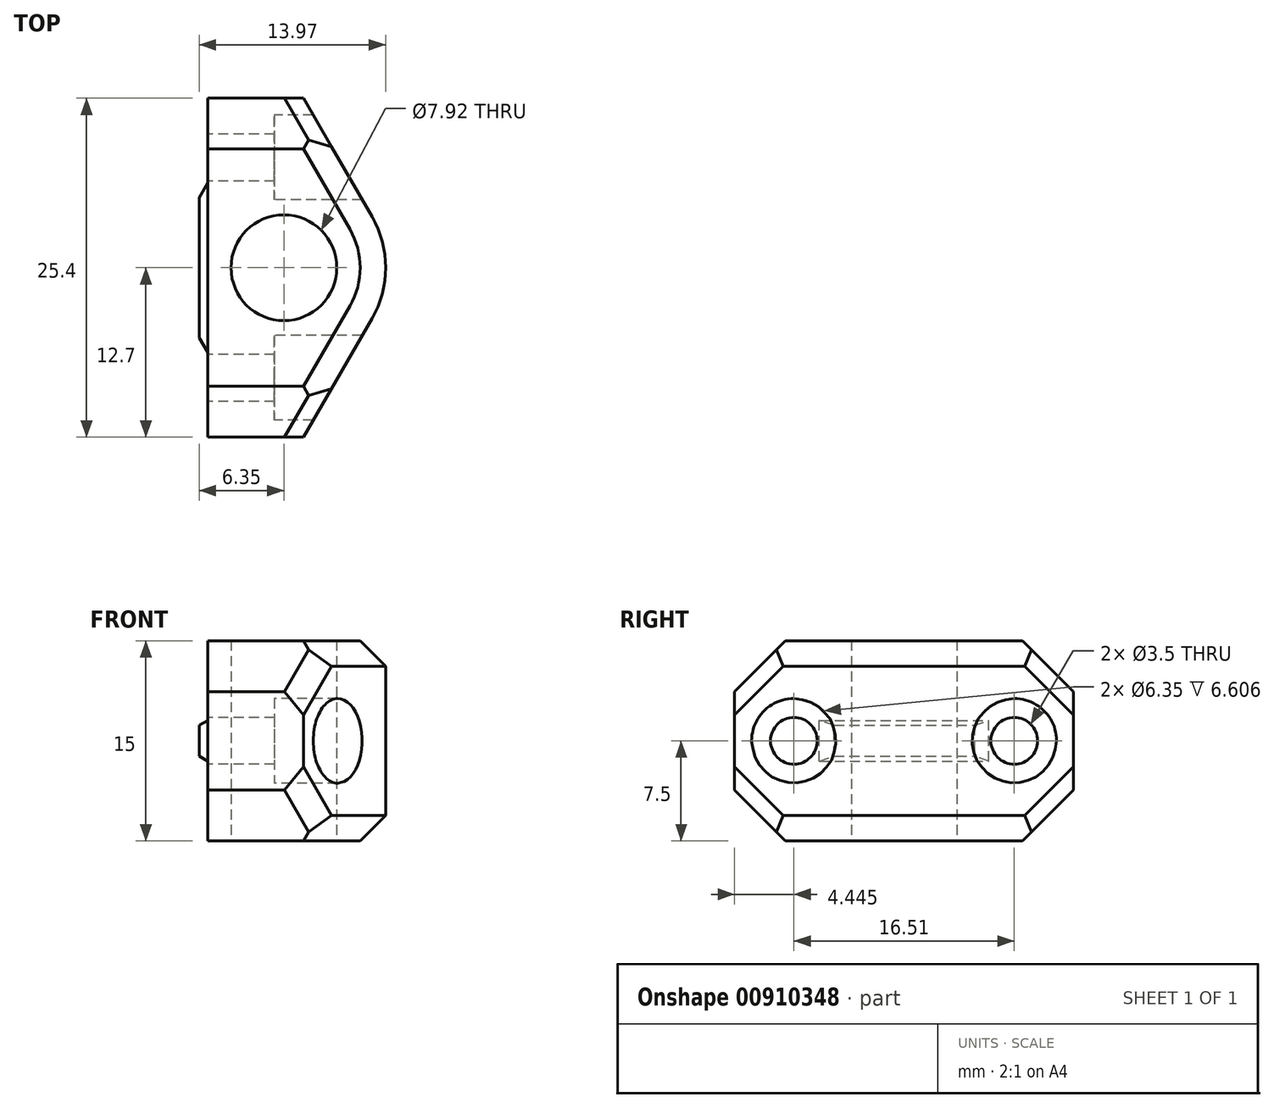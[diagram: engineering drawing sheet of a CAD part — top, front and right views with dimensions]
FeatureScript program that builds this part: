
annotation { "Feature Type Name" : "Feature", "Feature Type Description" : "" }
export const myFeature = defineFeature(function(context is Context, id is Id, definition is map)
    precondition{}
    {
        {
            var Q0;
            Q0=qCreatedBy(makeId("Top.planeOp"),FACE);
            var sketch = newSketch(context, id + "F0", { "sketchPlane" : qUnion([Q0])});
            skCircle(sketch, "E0", {"center": v(0, 0) * mm, "radius": 3.96 * mm});
            skLineSegment(sketch, "E1", {"start": v(-5.72, 12.7) * mm, "end": v(-5.72, -12.7) * mm});
            skLineSegment(sketch, "E2", {"start": v(-5.72, -12.7) * mm, "end": v(1.47, -12.7) * mm});
            skLineSegment(sketch, "E3", {"start": v(1.47, -12.7) * mm, "end": v(6.6, -3.81) * mm});
            skLineSegment(sketch, "E4", {"start": v(6.6, 3.8) * mm, "end": v(1.47, 12.7) * mm});
            skLineSegment(sketch, "E5", {"start": v(1.47, 12.7) * mm, "end": v(-5.72, 12.7) * mm});
            skArc(sketch, "E6", {"start": v(6.6, -3.81) * mm, "mid": v(7.62, 0) * mm, "end": v(6.6, 3.8) * mm});
            skLineSegment(sketch, "E7", {"start": v(-5.72, 6.6) * mm, "end": v(-0.72, 6.6) * mm, "construction": true});
            skLineSegment(sketch, "E8", {"start": v(-0.72, 6.6) * mm, "end": v(-0.72, 5.08) * mm, "construction": true});
            skLineSegment(sketch, "E9", {"start": v(-0.72, 5.08) * mm, "end": v(5.87, 5.08) * mm, "construction": true});
            skLineSegment(sketch, "E10", {"start": v(-5.72, 9.9) * mm, "end": v(-0.72, 9.9) * mm, "construction": true});
            skLineSegment(sketch, "E11", {"start": v(-0.72, 9.9) * mm, "end": v(-0.72, 11.43) * mm, "construction": true});
            skLineSegment(sketch, "E12", {"start": v(-0.72, 11.43) * mm, "end": v(2.2, 11.43) * mm, "construction": true});
            skLineSegment(sketch, "E13", {"start": v(-0.72, 9.9) * mm, "end": v(-0.72, 6.6) * mm, "construction": true});
            skLineSegment(sketch, "E14", {"start": v(-0.72, 8.26) * mm, "end": v(-5.72, 8.26) * mm, "construction": true});
            skSolve(sketch);
        }
        {
            var Q0;
            Q0 = qSketchRegion(id + "F0", true);
            extrude(context, id + "F1", {"entities" : qUnion([Q0]), "depth" : 15 * mm, "offsetDistance" : 25.4 * mm, "symmetric" : true});
        }
        {
            var Q0;
            Q0=makeQuery(id+"F1.opExtrude","SWEPT_FACE",FACE,{"disambiguationData":[OSD([sQuery(id+"F0.wireOp",EDGE,"E1")])]});
            var sketch = newSketch(context, id + "F2", { "sketchPlane" : qUnion([Q0])});
            skPoint(sketch, "E15", {"position": v(-8.26, 0) * mm});
            skPoint(sketch, "E16", {"position": v(8.26, 0) * mm});
            skLineSegment(sketch, "E17", {"start": v(-8.26, 0) * mm, "end": v(8.26, 0) * mm, "construction": true});
            skCircle(sketch, "E18", {"center": v(8.26, 0) * mm, "radius": 1.75 * mm});
            skCircle(sketch, "E19", {"center": v(-8.26, 0) * mm, "radius": 1.75 * mm});
            skSolve(sketch);
        }
        {
            var Q0;
            Q0 = qSketchRegion(id + "F2", true);
            extrude(context, id + "F3", {"entities" : qUnion([Q0]), "operationType" : NewBodyOperationType.REMOVE, "oppositeDirection" : true, "depth" : 5 * mm, "offsetDistance" : 25.4 * mm});
        }
        {
            var Q0;
            Q0=makeQuery(id+"F3.boolean.opBoolean","COPY",FACE,{"derivedFrom":makeQuery(id+"F3.opExtrude","CAP_FACE",FACE,{"disambiguationData":[OSD([sQuery(id+"F2.wireOp",EDGE,"E18")])],"isStart":false})});
            var sketch = newSketch(context, id + "F4", { "sketchPlane" : qUnion([Q0])});
            skCircle(sketch, "E20", {"center": v(8.26, 0) * mm, "radius": 3.18 * mm});
            skCircle(sketch, "E21", {"center": v(-8.26, 0) * mm, "radius": 3.18 * mm});
            skSolve(sketch);
        }
        {
            var Q0;
            Q0 = qSketchRegion(id + "F4", true);
            extrude(context, id + "F5", {"entities" : qUnion([Q0]), "operationType" : NewBodyOperationType.REMOVE, "endBound" : BoundingType.THROUGH_ALL, "oppositeDirection" : true, "depth" : 25.4 * mm, "offsetDistance" : 25.4 * mm});
        }
        {
            var Q0;
            Q0=makeQuery(id+"F1.opExtrude","CAP_EDGE",EDGE,{"disambiguationData":[OSD([sQuery(id+"F0.wireOp",EDGE,"E5")])],"isStart":true});
            var Q1;
            Q1=makeQuery(id+"F1.opExtrude","CAP_EDGE",EDGE,{"disambiguationData":[OSD([sQuery(id+"F0.wireOp",EDGE,"E5")])],"isStart":false});
            var Q2;
            Q2=makeQuery(id+"F1.opExtrude","CAP_EDGE",EDGE,{"disambiguationData":[OSD([sQuery(id+"F0.wireOp",EDGE,"E2")])],"isStart":false});
            var Q3;
            Q3=makeQuery(id+"F1.opExtrude","CAP_EDGE",EDGE,{"disambiguationData":[OSD([sQuery(id+"F0.wireOp",EDGE,"E2")])],"isStart":true});
            chamfer(context, id + "F6", {"entities" : qUnion([Q0, Q1, Q2, Q3]), "width" : 3.8 * mm, "tangentPropagation" : true});
        }
        {
            var Q0;
            Q0=makeQuery(id+"F1.opExtrude","CAP_EDGE",EDGE,{"disambiguationData":[OSD([sQuery(id+"F0.wireOp",EDGE,"E3")])],"isStart":true});
            var Q1;
            Q1=makeQuery(id+"F1.opExtrude","CAP_EDGE",EDGE,{"disambiguationData":[OSD([sQuery(id+"F0.wireOp",EDGE,"E3")])],"isStart":false});
            var Q2;
            Q2=makeQuery(id+"F6.opChamfer","BLEND_EDGE",EDGE,{"blendedFrom":[makeQuery(id+"F1.opExtrude","CAP_EDGE",EDGE,{"disambiguationData":[OSD([sQuery(id+"F0.wireOp",EDGE,"E2")])],"isStart":false}),makeQuery(id+"F1.opExtrude","SWEPT_FACE",FACE,{"disambiguationData":[OSD([sQuery(id+"F0.wireOp",EDGE,"E3")])]})],"blendedInto":[makeQuery(id+"F1.opExtrude","SWEPT_FACE",FACE,{"disambiguationData":[OSD([sQuery(id+"F0.wireOp",EDGE,"E3")])]})]});
            var Q3;
            Q3=makeQuery(id+"F6.opChamfer","BLEND_EDGE",EDGE,{"blendedFrom":[makeQuery(id+"F1.opExtrude","CAP_EDGE",EDGE,{"disambiguationData":[OSD([sQuery(id+"F0.wireOp",EDGE,"E2")])],"isStart":true}),makeQuery(id+"F1.opExtrude","SWEPT_FACE",FACE,{"disambiguationData":[OSD([sQuery(id+"F0.wireOp",EDGE,"E3")])]})],"blendedInto":[makeQuery(id+"F1.opExtrude","SWEPT_FACE",FACE,{"disambiguationData":[OSD([sQuery(id+"F0.wireOp",EDGE,"E3")])]})]});
            var Q4;
            Q4=makeQuery(id+"F6.opChamfer","BLEND_EDGE",EDGE,{"blendedFrom":[makeQuery(id+"F1.opExtrude","CAP_EDGE",EDGE,{"disambiguationData":[OSD([sQuery(id+"F0.wireOp",EDGE,"E5")])],"isStart":true}),makeQuery(id+"F1.opExtrude","SWEPT_FACE",FACE,{"disambiguationData":[OSD([sQuery(id+"F0.wireOp",EDGE,"E4")])]})],"blendedInto":[makeQuery(id+"F1.opExtrude","SWEPT_FACE",FACE,{"disambiguationData":[OSD([sQuery(id+"F0.wireOp",EDGE,"E4")])]})]});
            var Q5;
            Q5=makeQuery(id+"F6.opChamfer","BLEND_EDGE",EDGE,{"blendedFrom":[makeQuery(id+"F1.opExtrude","CAP_EDGE",EDGE,{"disambiguationData":[OSD([sQuery(id+"F0.wireOp",EDGE,"E5")])],"isStart":false}),makeQuery(id+"F1.opExtrude","SWEPT_FACE",FACE,{"disambiguationData":[OSD([sQuery(id+"F0.wireOp",EDGE,"E4")])]})],"blendedInto":[makeQuery(id+"F1.opExtrude","SWEPT_FACE",FACE,{"disambiguationData":[OSD([sQuery(id+"F0.wireOp",EDGE,"E4")])]})]});
            chamfer(context, id + "F7", {"entities" : qUnion([Q0, Q1, Q2, Q3, Q4, Q5]), "width" : 1.9 * mm, "tangentPropagation" : true});
        }
        {
            var Q0;
            Q0=qCreatedBy(makeId("Front.planeOp"),FACE);
            var sketch = newSketch(context, id + "F8", { "sketchPlane" : qUnion([Q0])});
            skLineSegment(sketch, "E22", {"start": v(-5.72, 1.52) * mm, "end": v(-6.35, 1.16) * mm});
            skLineSegment(sketch, "E23", {"start": v(-6.35, 1.16) * mm, "end": v(-6.35, -1.16) * mm});
            skLineSegment(sketch, "E24", {"start": v(-6.35, -1.16) * mm, "end": v(-5.72, -1.52) * mm});
            skLineSegment(sketch, "E25", {"start": v(-5.72, -1.52) * mm, "end": v(-5.72, 1.52) * mm});
            skLineSegment(sketch, "E26", {"start": v(0, 0) * mm, "end": v(-5.72, 0) * mm, "construction": true});
            skPoint(sketch, "E26.endSnap0", {"position": v(-5.72, 0) * mm});
            skSolve(sketch);
        }
        {
            var Q0;
            Q0 = qSketchRegion(id + "F8", true);
            extrude(context, id + "F9", {"entities" : qUnion([Q0]), "operationType" : NewBodyOperationType.ADD, "depth" : 12.7 * mm, "offsetDistance" : 25.4 * mm, "symmetric" : true});
        }
        {
            var Q0;
            Q0=makeQuery(id+"F9.opExtrude","CAP_EDGE",EDGE,{"disambiguationData":[OSD([sQuery(id+"F8.wireOp",EDGE,"E23")])],"isStart":false});
            var Q1;
            Q1=makeQuery(id+"F9.opExtrude","CAP_EDGE",EDGE,{"disambiguationData":[OSD([sQuery(id+"F8.wireOp",EDGE,"E23")])],"isStart":true});
            chamfer(context, id + "F10", {"entities" : qUnion([Q0, Q1]), "chamferType" : ChamferType.OFFSET_ANGLE, "width" : 0.64 * mm, "oppositeDirection" : false, "angle" : 60 * degree, "tangentPropagation" : true});
        }
    });
